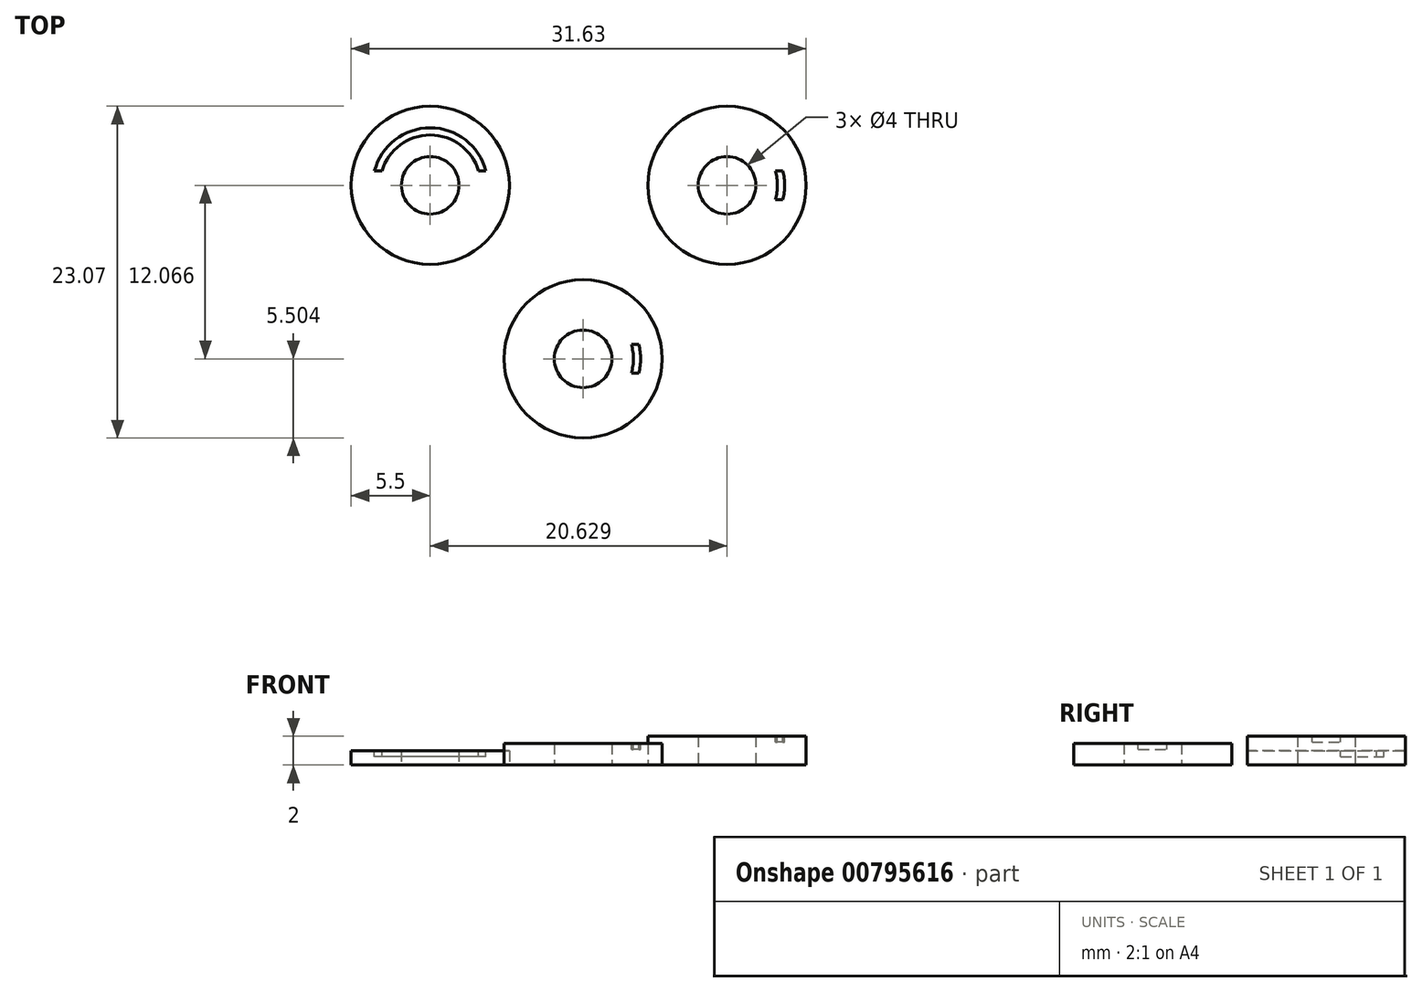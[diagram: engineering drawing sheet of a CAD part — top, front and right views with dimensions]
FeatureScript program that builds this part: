
annotation { "Feature Type Name" : "Feature", "Feature Type Description" : "" }
export const myFeature = defineFeature(function(context is Context, id is Id, definition is map)
    precondition{}
    {
        {
            var Q0;
            Q0=qCreatedBy(makeId("Top.planeOp"),FACE);
            var sketch = newSketch(context, id + "F0", { "sketchPlane" : qUnion([Q0])});
            skCircle(sketch, "E0", {"center": v(0, 0) * mm, "radius": 2 * mm});
            skCircle(sketch, "E1", {"center": v(0, 0) * mm, "radius": 5.5 * mm});
            skSolve(sketch);
        }
        {
            var Q0;
            Q0=makeQuery(id+"F0.imprint","IMPRINT",FACE,{"disambiguationData":[TD([[makeQuery(id+"F0.imprint","IMPRINT",EDGE,{"derivedFrom":sQuery(id+"F0.wireOp",EDGE,"E0")}),-1.0]])]});
            extrude(context, id + "F1", {"entities" : qUnion([Q0]), "depth" : 1 * mm, "offsetDistance" : 25 * mm});
        }
        {
            var Q0;
            Q0=makeQuery(id+"F1.opExtrude","CAP_FACE",FACE,{"disambiguationData":[OSD([sQuery(id+"F0.wireOp",EDGE,"E0"),sQuery(id+"F0.wireOp",EDGE,"E1")])],"isStart":false});
            var sketch = newSketch(context, id + "F2", { "sketchPlane" : qUnion([Q0])});
            skCircle(sketch, "E2", {"center": v(0, 0) * mm, "radius": 4 * mm});
            skCircle(sketch, "E3", {"center": v(0, 0) * mm, "radius": 3.5 * mm});
            skLineSegment(sketch, "E4.bottom", {"start": v(7.5, 1) * mm, "end": v(-7.5, 1) * mm});
            skLineSegment(sketch, "E4.top", {"start": v(7.5, -1) * mm, "end": v(-7.5, -1) * mm});
            skLineSegment(sketch, "E4.left", {"start": v(7.5, 1) * mm, "end": v(7.5, -1) * mm});
            skLineSegment(sketch, "E4.right", {"start": v(-7.5, 1) * mm, "end": v(-7.5, -1) * mm});
            skSolve(sketch);
        }
        {
            var Q0;
            {var subQ0=sQuery(id+"F2.wireOp",EDGE,"E4.bottom");var subQ1=sQuery(id+"F2.wireOp",EDGE,"E2");var subQ2=makeQuery(id+"F2.imprint","INTERSECT",VERTEX,{"disambiguationData":[OD(0.0)],"derivedFrom":[subQ1,subQ0]});Q0=makeQuery(id+"F2.imprint","IMPRINT",FACE,{"disambiguationData":[TD([[makeQuery(id+"F2.imprint","IMPRINT",EDGE,{"disambiguationData":[TD([[subQ2,1.0]])],"derivedFrom":subQ1}),1.0]])]});}
            extrude(context, id + "F3", {"entities" : qUnion([Q0]), "operationType" : NewBodyOperationType.REMOVE, "oppositeDirection" : true, "depth" : 0.4 * mm, "offsetDistance" : 25 * mm});
        }
        {
            var Q0;
            Q0=qCreatedBy(makeId("Top.planeOp"),FACE);
            var sketch = newSketch(context, id + "F4", { "sketchPlane" : qUnion([Q0])});
            skCircle(sketch, "E5", {"center": v(20.63, 0) * mm, "radius": 2 * mm});
            skCircle(sketch, "E6", {"center": v(20.63, 0) * mm, "radius": 5.5 * mm});
            skSolve(sketch);
        }
        {
            var Q0;
            Q0 = qSketchRegion(id + "F4", true);
            extrude(context, id + "F5", {"entities" : qUnion([Q0]), "depth" : 2 * mm, "offsetDistance" : 25 * mm});
        }
        {
            var Q0;
            Q0=makeQuery(id+"F5.opExtrude","CAP_FACE",FACE,{"disambiguationData":[OSD([sQuery(id+"F4.wireOp",EDGE,"E5"),sQuery(id+"F4.wireOp",EDGE,"E6")])],"isStart":false});
            var sketch = newSketch(context, id + "F6", { "sketchPlane" : qUnion([Q0])});
            skCircle(sketch, "E7", {"center": v(20.63, 0) * mm, "radius": 3.5 * mm});
            skCircle(sketch, "E8", {"center": v(20.63, 0) * mm, "radius": 4 * mm});
            skLineSegment(sketch, "E9.bottom", {"start": v(28.13, 1) * mm, "end": v(13.13, 1) * mm});
            skLineSegment(sketch, "E9.top", {"start": v(28.13, -1) * mm, "end": v(13.13, -1) * mm});
            skLineSegment(sketch, "E9.left", {"start": v(28.13, 1) * mm, "end": v(28.13, -1) * mm});
            skLineSegment(sketch, "E9.right", {"start": v(13.13, 1) * mm, "end": v(13.13, -1) * mm});
            skSolve(sketch);
        }
        {
            var Q0;
            {var subQ0=sQuery(id+"F6.wireOp",EDGE,"E9.bottom");var subQ1=sQuery(id+"F6.wireOp",EDGE,"E7");var subQ2=makeQuery(id+"F6.imprint","INTERSECT",VERTEX,{"disambiguationData":[OD(0.0)],"derivedFrom":[subQ1,subQ0]});Q0=makeQuery(id+"F6.imprint","IMPRINT",FACE,{"disambiguationData":[TD([[makeQuery(id+"F6.imprint","IMPRINT",EDGE,{"disambiguationData":[TD([[subQ2,1.0]])],"derivedFrom":subQ1}),-1.0]])]});}
            var Q1;
            {var subQ0=sQuery(id+"F6.wireOp",EDGE,"E9.top");var subQ1=sQuery(id+"F6.wireOp",EDGE,"E7");var subQ2=makeQuery(id+"F6.imprint","INTERSECT",VERTEX,{"disambiguationData":[OD(0.0)],"derivedFrom":[subQ1,subQ0]});Q1=makeQuery(id+"F6.imprint","IMPRINT",FACE,{"disambiguationData":[TD([[makeQuery(id+"F6.imprint","IMPRINT",EDGE,{"disambiguationData":[TD([[subQ2,-1.0]])],"derivedFrom":subQ1}),-1.0]])]});}
            extrude(context, id + "F7", {"entities" : qUnion([Q0, Q1]), "operationType" : NewBodyOperationType.REMOVE, "oppositeDirection" : true, "depth" : 0.4 * mm, "offsetDistance" : 25 * mm});
        }
        {
            var Q0;
            Q0=qCreatedBy(makeId("Top.planeOp"),FACE);
            var sketch = newSketch(context, id + "F8", { "sketchPlane" : qUnion([Q0])});
            skCircle(sketch, "E10", {"center": v(10.62, -12.07) * mm, "radius": 2 * mm});
            skCircle(sketch, "E11", {"center": v(10.62, -12.07) * mm, "radius": 5.5 * mm});
            skSolve(sketch);
        }
        {
            var Q0;
            Q0=makeQuery(id+"F8.imprint","IMPRINT",FACE,{"disambiguationData":[TD([[makeQuery(id+"F8.imprint","IMPRINT",EDGE,{"derivedFrom":sQuery(id+"F8.wireOp",EDGE,"E10")}),-1.0]])]});
            extrude(context, id + "F9", {"entities" : qUnion([Q0]), "depth" : 1.5 * mm, "offsetDistance" : 25 * mm});
        }
        {
            var Q0;
            Q0=makeQuery(id+"F9.opExtrude","CAP_FACE",FACE,{"disambiguationData":[OSD([sQuery(id+"F8.wireOp",EDGE,"E10"),sQuery(id+"F8.wireOp",EDGE,"E11")])],"isStart":false});
            var sketch = newSketch(context, id + "F10", { "sketchPlane" : qUnion([Q0])});
            skCircle(sketch, "E12", {"center": v(10.62, -12.07) * mm, "radius": 4 * mm});
            skCircle(sketch, "E13", {"center": v(10.62, -12.07) * mm, "radius": 3.5 * mm});
            skLineSegment(sketch, "E14.bottom", {"start": v(18.12, -11.07) * mm, "end": v(3.12, -11.07) * mm});
            skLineSegment(sketch, "E14.top", {"start": v(18.12, -13.07) * mm, "end": v(3.12, -13.07) * mm});
            skLineSegment(sketch, "E14.left", {"start": v(18.12, -11.07) * mm, "end": v(18.12, -13.07) * mm});
            skLineSegment(sketch, "E14.right", {"start": v(3.12, -11.07) * mm, "end": v(3.12, -13.07) * mm});
            skLineSegment(sketch, "E15", {"start": v(9.62, -11.07) * mm, "end": v(9.62, -19.97) * mm});
            skSolve(sketch);
        }
        {
            var Q0;
            {var subQ0=sQuery(id+"F10.wireOp",EDGE,"E14.bottom");var subQ1=sQuery(id+"F10.wireOp",EDGE,"E12");var subQ2=makeQuery(id+"F10.imprint","INTERSECT",VERTEX,{"disambiguationData":[OD(0.0)],"derivedFrom":[subQ1,subQ0]});Q0=makeQuery(id+"F10.imprint","IMPRINT",FACE,{"disambiguationData":[TD([[makeQuery(id+"F10.imprint","IMPRINT",EDGE,{"disambiguationData":[TD([[subQ2,1.0]])],"derivedFrom":subQ1}),1.0]])]});}
            var Q1;
            {var subQ0=sQuery(id+"F10.wireOp",EDGE,"E14.top");var subQ1=sQuery(id+"F10.wireOp",EDGE,"E12");var subQ2=makeQuery(id+"F10.imprint","INTERSECT",VERTEX,{"disambiguationData":[OD(0.0)],"derivedFrom":[subQ1,subQ0]});Q1=makeQuery(id+"F10.imprint","IMPRINT",FACE,{"disambiguationData":[TD([[makeQuery(id+"F10.imprint","IMPRINT",EDGE,{"disambiguationData":[TD([[subQ2,-1.0]])],"derivedFrom":subQ1}),1.0]])]});}
            extrude(context, id + "F11", {"entities" : qUnion([Q0, Q1]), "operationType" : NewBodyOperationType.REMOVE, "oppositeDirection" : true, "depth" : 0.4 * mm, "offsetDistance" : 25 * mm});
        }
    });
